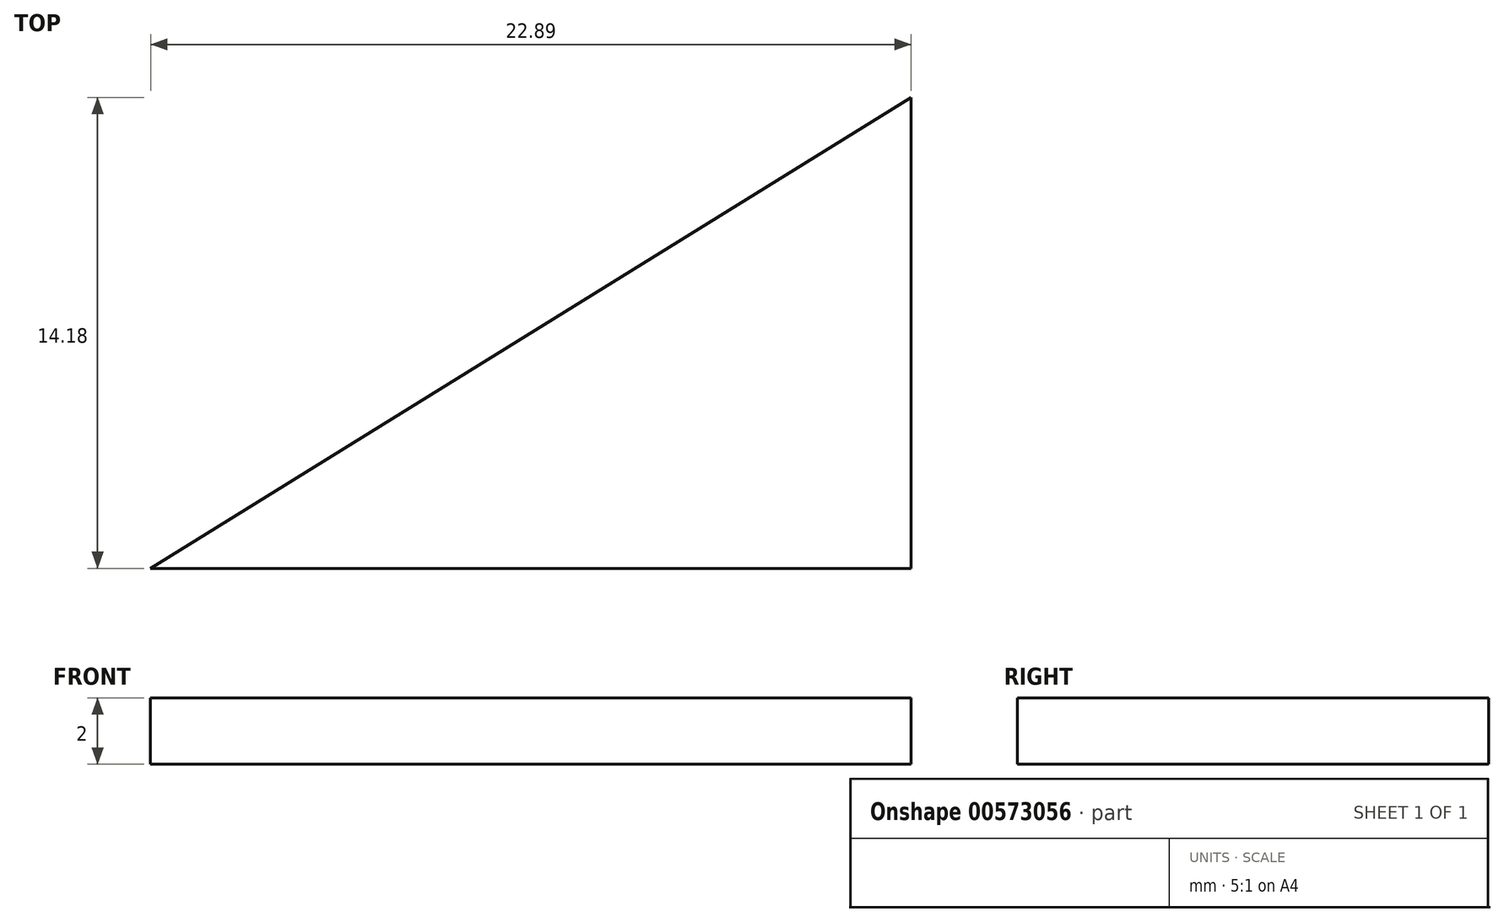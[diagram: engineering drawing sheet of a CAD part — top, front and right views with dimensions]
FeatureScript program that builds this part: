
annotation { "Feature Type Name" : "Feature", "Feature Type Description" : "" }
export const myFeature = defineFeature(function(context is Context, id is Id, definition is map)
    precondition{}
    {
        {
            var Q0;
            Q0=qCreatedBy(makeId("Top.planeOp"),FACE);
            var sketch = newSketch(context, id + "F0", { "sketchPlane" : qUnion([Q0])});
            skLineSegment(sketch, "E0", {"start": v(-24.94, 33.03) * mm, "end": v(-47.83, 18.85) * mm});
            skLineSegment(sketch, "E1", {"start": v(-47.83, 18.85) * mm, "end": v(-24.94, 18.85) * mm});
            skLineSegment(sketch, "E2", {"start": v(-24.94, 18.85) * mm, "end": v(-24.94, 33.03) * mm});
            skSolve(sketch);
        }
        {
            var Q0;
            Q0=makeQuery(id+"F0.imprint","IMPRINT",FACE,{"disambiguationData":[TD([[makeQuery(id+"F0.imprint","IMPRINT",EDGE,{"derivedFrom":sQuery(id+"F0.wireOp",EDGE,"E0")}),1.0]])]});
            extrude(context, id + "F1", {"entities" : qUnion([Q0]), "depth" : 2 * mm, "offsetDistance" : 25 * mm});
        }
    });
